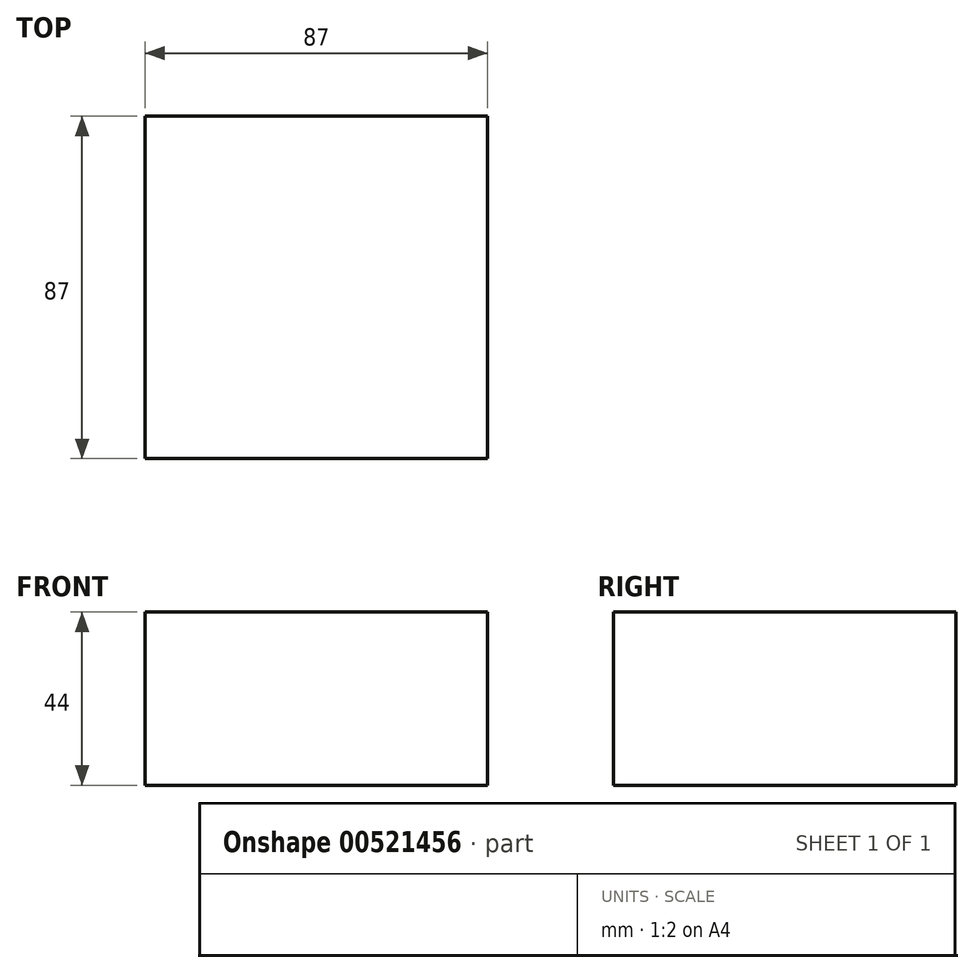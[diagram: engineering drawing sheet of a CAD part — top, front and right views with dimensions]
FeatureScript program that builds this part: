
annotation { "Feature Type Name" : "Feature", "Feature Type Description" : "" }
export const myFeature = defineFeature(function(context is Context, id is Id, definition is map)
    precondition{}
    {
        {
            var Q0;
            Q0=qCreatedBy(makeId("Front.planeOp"),FACE);
            var sketch = newSketch(context, id + "F0", { "sketchPlane" : qUnion([Q0])});
            skLineSegment(sketch, "E0.bottom", {"start": v(43.5, 22) * mm, "end": v(-43.5, 22) * mm});
            skLineSegment(sketch, "E0.top", {"start": v(43.5, -22) * mm, "end": v(-43.5, -22) * mm});
            skLineSegment(sketch, "E0.left", {"start": v(43.5, 22) * mm, "end": v(43.5, -22) * mm});
            skLineSegment(sketch, "E0.right", {"start": v(-43.5, 22) * mm, "end": v(-43.5, -22) * mm});
            skPoint(sketch, "E0.middle", {"position": v(0, 0) * mm});
            skSolve(sketch);
        }
        {
            var Q0;
            Q0 = qSketchRegion(id + "F0", true);
            extrude(context, id + "F1", {"entities" : qUnion([Q0]), "depth" : 87 * mm, "offsetDistance" : 25 * mm});
        }
    });
